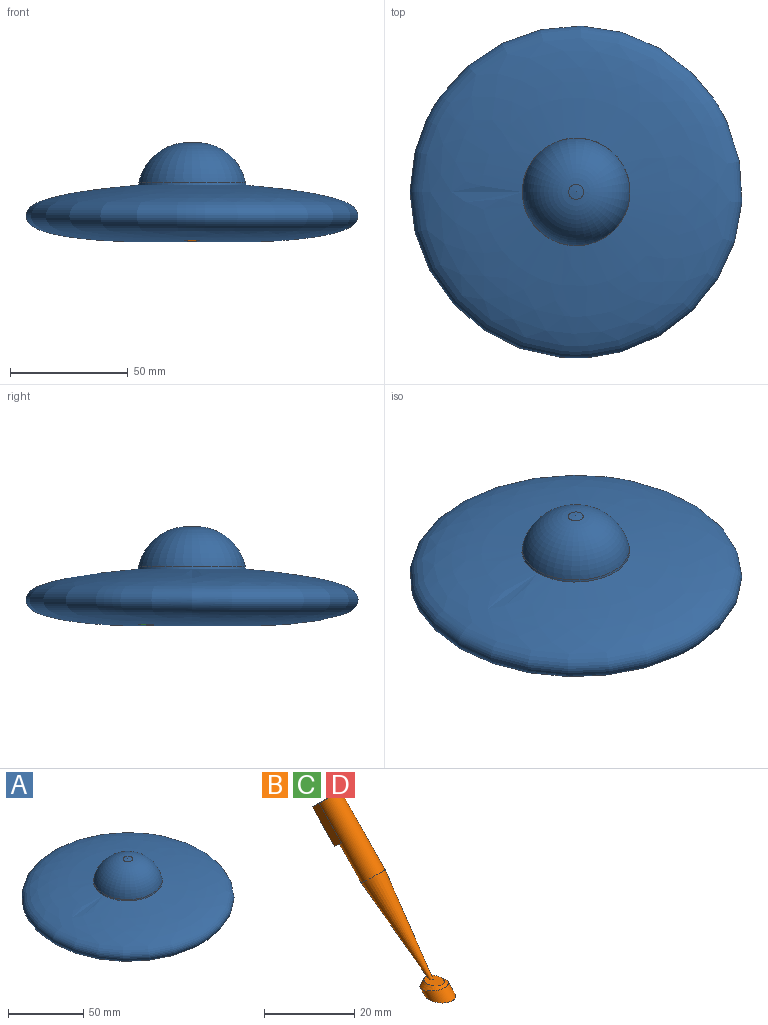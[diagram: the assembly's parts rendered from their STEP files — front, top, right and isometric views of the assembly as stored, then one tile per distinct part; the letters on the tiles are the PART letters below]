
ASSEMBLY  parts=4 mates=1
PART A: 59 faces, bbox 141.1x141.1x45.8 mm
  f0: revolved ~3.93x2.85mm, area 2.6mm2, adj f17,f48
  f1: revolved ~4.06x1.08mm, area 2.6mm2, adj f17,f30
  f2: revolved ~3.94x2.83mm, area 2.6mm2, adj f17,f39
  f3: revolved ~8.48x7.14mm, area 3mm2, adj f11,f46,f47,f48
  f4: revolved ~134.88x134.88mm, area 27236.8mm2, adj f10,f17,f24,f25,f26,f31,f33,f34
  f5: revolved ~4.4x4.29mm, area 2.3mm2, adj f11,f45,f46
  f6: revolved ~8.58x6.65mm, area 3mm2, adj f12,f37,f38,f39
  f7: revolved ~4.49x4.41mm, area 2.3mm2, adj f12,f36,f37
  f8: revolved ~8.04x3.8mm, area 3mm2, adj f13,f28,f29,f30
  f9: revolved ~3.49x3.25mm, area 2.3mm2, adj f13,f27,f28
  f10: plane 34.05x34.05mm, normal (0,0,1), area 910.4mm2, adj f4
  f11: cylinder r=3mm len=10.66mm, axis (0.6,-0.35,0.72), area 74.2mm2, adj f3,f5,f14,f41
  f12: cylinder r=3mm len=10.66mm, axis (-0.6,-0.35,0.72), area 74.2mm2, adj f6,f7,f14,f32
  f13: cylinder r=3mm len=10.66mm, axis (0,0.69,0.72), area 74.2mm2, adj f8,f9,f14,f23
  f14: revolved ~140.92x140.92mm, area 31628mm2, adj f11,f12,f13,f15,f20
  f15: plane 34.01x34.01mm, normal (0,0,-1), area 908.3mm2, adj f14
  f16: cone r=19.74mm half-angle=43.8deg, axis (0,0,-1), area 512.9mm2, adj f17,f19
  f17: cone r=22.42mm half-angle=52.3deg, axis (0,0,1), area 81.6mm2, adj f0,f1,f2,f4,f16,f30,f31,f39
  f18: plane 6.03x6.03mm, normal (0,0,-1), area 28.5mm2, adj f19
  f19: torus R=1.79mm, axis (0,0,1), area 1964.1mm2, adj f16,f18
  f20: cone r=22.67mm half-angle=11.3deg, axis (0,0,-1), area 136.3mm2, adj f14,f22
  f21: cone r=3.21mm half-angle=86.2deg, axis (0,0,-1), area 32.5mm2, adj f22
  f22: torus R=1.79mm, axis (0,0,1), area 2595.6mm2, adj f20,f21
  f23: revolved ~4.66x3.37mm, area 0.2mm2, adj f13,f27,f30
  f24: plane 32.8x32.79mm, normal (-1,0,0), area 227.3mm2, adj f4,f25,f31,f44,f57
  f25: plane 28.79x27.72mm, normal (0,0.72,-0.69), area 423.7mm2, adj f4,f24,f26,f34,f43,f44,f57
  f26: plane 32.79x32.74mm, normal (1,0,0), area 226.4mm2, adj f4,f25,f31,f33,f34,f57,f58
  f27: plane 33.28x32.52mm, normal (-1,0,0), area 130.6mm2, adj f9,f23,f28,f30,f57
  f28: plane 30.48x29.35mm, normal (0,-0.72,0.69), area 253.3mm2, adj f8,f9,f27,f29,f57
  f29: plane 33.3x32.53mm, normal (1,0,0), area 130.6mm2, adj f8,f28,f30,f57
  f30: cylinder r=3mm len=36.2mm, axis (0,0.69,0.72), area 365.4mm2, adj f1,f8,f17,f23,f27,f29,f52,f53
  f31: cylinder r=5.5mm len=39.4mm, axis (0,0.69,0.72), area 525.3mm2, adj f4,f17,f24,f26,f52,f53,f57
  f32: revolved ~5.53x5.11mm, area 0.2mm2, adj f12,f36,f39
  f33: plane 32.79x28.43mm, normal (0.5,-0.87,0), area 227.3mm2, adj f4,f26,f34,f40,f58
  f34: plane 28.79x27.33mm, normal (-0.62,-0.36,-0.69), area 423.7mm2, adj f4,f25,f26,f33,f35,f43,f58
  f35: plane 32.79x28.38mm, normal (-0.5,0.87,0), area 226.4mm2, adj f4,f34,f40,f42,f43,f56,f58
  f36: plane 32.52x28.83mm, normal (0.5,-0.87,0), area 130.6mm2, adj f7,f32,f37,f39,f58
  f37: plane 30.48x28.42mm, normal (0.62,0.36,0.69), area 253.3mm2, adj f6,f7,f36,f38,f58
  f38: plane 32.53x28.84mm, normal (-0.5,0.87,0), area 130.6mm2, adj f6,f37,f39,f58
  f39: cylinder r=3mm len=36.2mm, axis (-0.6,-0.35,0.72), area 365.4mm2, adj f2,f6,f17,f32,f36,f38,f54,f55
  f40: cylinder r=5.5mm len=39.4mm, axis (-0.6,-0.35,0.72), area 525.3mm2, adj f4,f17,f33,f35,f54,f55,f58
  f41: revolved ~5.49x4.91mm, area 0.2mm2, adj f11,f45,f48
  f42: plane 32.79x28.43mm, normal (0.5,0.87,0), area 227.3mm2, adj f4,f35,f43,f49,f56
  f43: plane 28.79x27.39mm, normal (0.62,-0.36,-0.69), area 423.7mm2, adj f4,f25,f34,f35,f42,f44,f56
  f44: plane 32.79x28.38mm, normal (-0.5,-0.87,0), area 226.4mm2, adj f4,f24,f25,f43,f49,f56,f57
  f45: plane 32.52x28.83mm, normal (0.5,0.87,0), area 130.6mm2, adj f5,f41,f46,f48,f56
  f46: plane 30.48x28.42mm, normal (-0.62,0.36,0.69), area 253.3mm2, adj f3,f5,f45,f47,f56
  f47: plane 32.53x28.84mm, normal (-0.5,-0.87,0), area 130.6mm2, adj f3,f46,f48,f56
  f48: cylinder r=3mm len=36.2mm, axis (0.6,-0.35,0.72), area 365.4mm2, adj f0,f3,f17,f41,f45,f47,f50,f51
  f49: cylinder r=5.5mm len=39.4mm, axis (0.6,-0.35,0.72), area 525.3mm2, adj f4,f17,f42,f44,f50,f51,f56
  f50: extruded ~16.25x15.17mm, area 75.6mm2, adj f17,f48,f49,f56
  f51: extruded ~16.24x15.24mm, area 75.6mm2, adj f17,f48,f49,f56
  f52: extruded ~16.25x15.64mm, area 75.6mm2, adj f17,f30,f31,f57
  f53: extruded ~16.24x15.64mm, area 75.6mm2, adj f17,f30,f31,f57
  f54: extruded ~16.25x15.24mm, area 75.6mm2, adj f17,f39,f40,f58
  f55: extruded ~16.24x15.17mm, area 75.6mm2, adj f17,f39,f40,f58
  f56: plane 10.66x8.1mm, normal (0.6,-0.35,0.72), area 41.2mm2, adj f35,f42,f43,f44,f45,f46,f47,f48
  f57: plane 11x5.84mm, normal (0,0.69,0.72), area 41.2mm2, adj f24,f25,f26,f27,f28,f29,f30,f31
  f58: plane 10.69x8.05mm, normal (-0.6,-0.35,0.72), area 41.2mm2, adj f26,f33,f34,f35,f36,f37,f38,f39
PART B: 13 faces, bbox 6.6x40.8x42 mm
  f0: revolved ~5.11x4.14mm, area 14.8mm2, adj f1,f2,f10
  f1: revolved ~0.73x0.53mm, area 0.5mm2, adj f0,f2
  f2: cone r=3mm half-angle=5.7deg, axis (0,0.69,0.72), area 280.2mm2, adj f0,f1,f3
  f3: cylinder r=3mm len=18.57mm, axis (0,-0.69,-0.72), area 282.7mm2, adj f2,f4,f6,f7,f8,f9
  f4: plane 3x2.16mm, normal (0,-0.69,-0.72), area 1.9mm2, adj f3,f5,f6
  f5: plane 7.2x6.94mm, normal (0,0.72,-0.69), area 60mm2, adj f4,f6,f7,f8,f9
  f6: plane 9.28x9.1mm, normal (-1,0,0), area 30mm2, adj f3,f4,f5,f7
  f7: plane 6x4.32mm, normal (0,0.69,0.72), area 32.1mm2, adj f3,f5,f6,f8
  f8: plane 9.28x9.1mm, normal (1,0,0), area 30mm2, adj f3,f5,f7,f9
  f9: plane 3x2.16mm, normal (0,-0.69,-0.72), area 1.9mm2, adj f3,f5,f8
  f10: bspline ~6.6x6mm, area 25mm2, adj f0,f11
  f11: cylinder r=3mm len=8.97mm, axis (0,-0.69,-0.72), area 47.6mm2, adj f10,f12
  f12: revolved ~7.92x6.62mm, area 36.9mm2, adj f11
PART C: same geometry as B
PART D: same geometry as B
PLACE A t=(1.84,4.45,0.79)mm
PLACE B t=(1.79,4.4,0.75)mm
PLACE C rot(axis=(0,0,-1),120deg) t=(1.83,4.52,0.75)mm
PLACE D rot(axis=(0,0,1),120deg) t=(1.91,4.42,0.75)mm
MATE slider B.f11 <-> A.f30  axis (0,-0.69,-0.72) through (1.79,-6.24,8.66)mm
